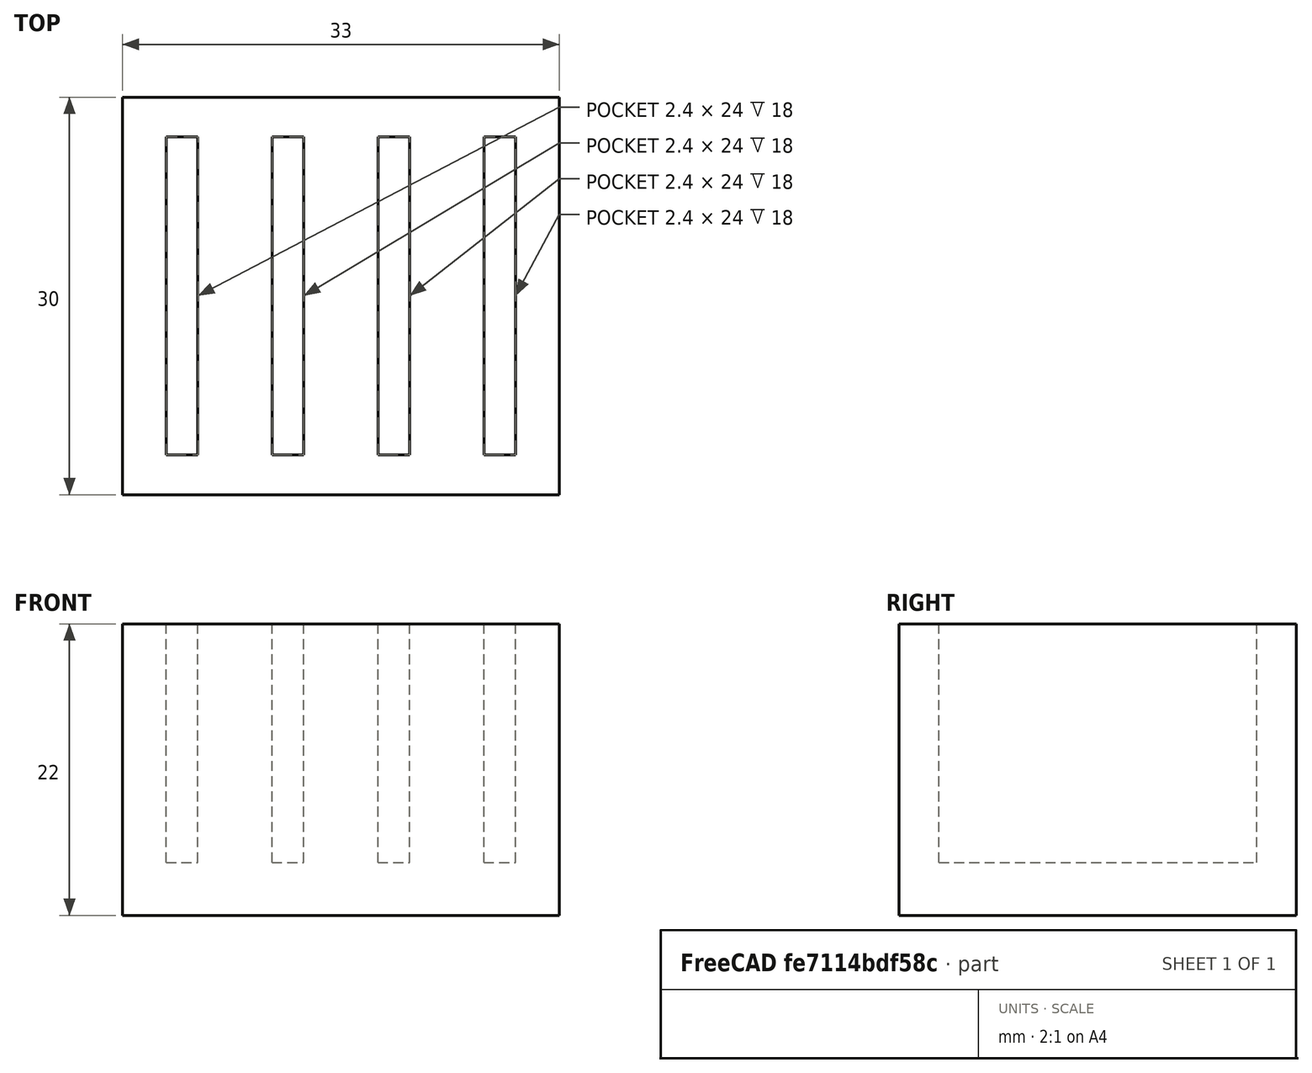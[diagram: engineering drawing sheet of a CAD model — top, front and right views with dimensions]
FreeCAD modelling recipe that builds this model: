
FCSTD DOCUMENT  (FreeCAD 1.0R39319 (Git))
Label: ojt1_t08_r01_sd_holder
License: All rights reserved
LicenseURL: https://en.wikipedia.org/wiki/All_rights_reserved
objects: Part::Box×5, Part::MultiFuse×1, Part::Cut×1
note: 7 computed .brp shape members not serialized (recipe doc carries the construction recipe); baked Part::Feature solids carry a one-line shape summary decoded from their .brp

FEATURE [Part::Box] Box  label="Base"
  AttacherType = Attacher::AttachEngine3D
  Height = 22
  Length = 33
  Placement = pos=(-16.5,0,0) rot=(0,0,1;0rad)
  Width = 30
FEATURE [Part::Box] Box001  label="Ranura_01"
  AttacherType = Attacher::AttachEngine3D
  Height = 20
  Length = 2.4
  Placement = pos=(0,-28,0) rot=(0,0,1;0rad)
  Width = 24
FEATURE [Part::Box] Box002  label="Ranura_002"
  AttacherType = Attacher::AttachEngine3D
  Height = 20
  Length = 2.4
  Placement = pos=(8,-28,0) rot=(0,0,1;0rad)
  Width = 24
FEATURE [Part::Box] Box003  label="Ranura_003"
  AttacherType = Attacher::AttachEngine3D
  Height = 20
  Length = 2.4
  Placement = pos=(16,-28,0) rot=(0,0,1;0rad)
  Width = 24
FEATURE [Part::Box] Box004  label="Ranura_004"
  AttacherType = Attacher::AttachEngine3D
  Height = 20
  Length = 2.4
  Placement = pos=(24,-28,0) rot=(0,0,1;0rad)
  Width = 24
FEATURE [Part::MultiFuse] Fusion
  Placement = pos=(-13.2,31,4) rot=(0,0,1;0rad)
  Refine = true
  Shapes = -> [Box001,Box002,Box003,Box004]
FEATURE [Part::Cut] Cut
  Base = -> Box
  Refine = true
  Tool = -> Fusion
